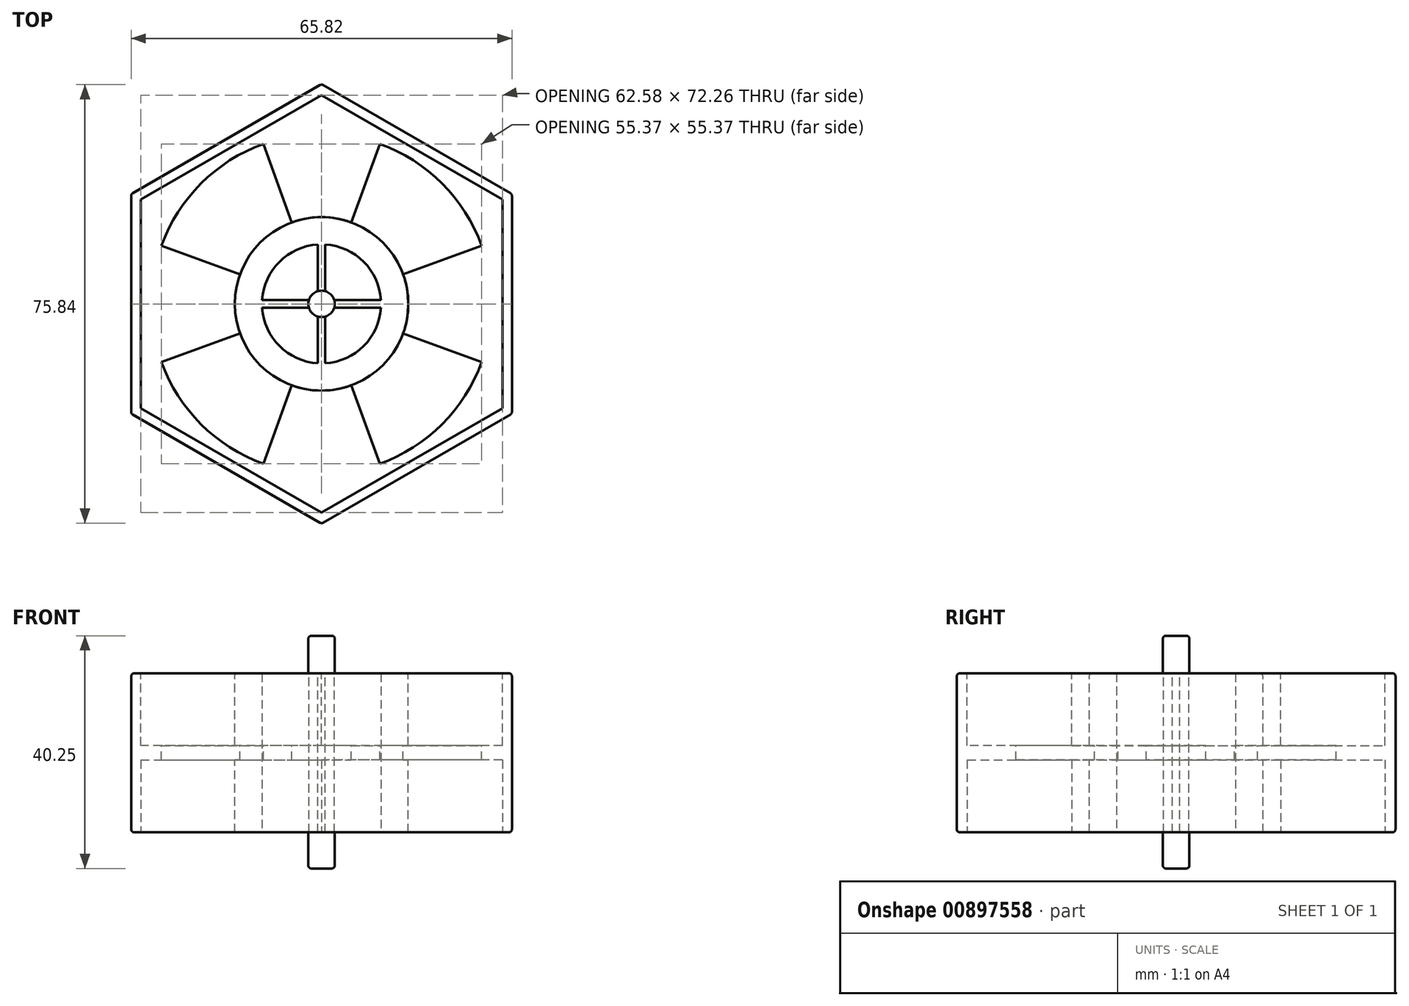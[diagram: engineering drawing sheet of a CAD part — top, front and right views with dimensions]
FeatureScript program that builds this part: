
annotation { "Feature Type Name" : "Feature", "Feature Type Description" : "" }
export const myFeature = defineFeature(function(context is Context, id is Id, definition is map)
    precondition{}
    {
        {
            var Q0;
            Q0=qCreatedBy(makeId("Top.planeOp"),FACE);
            var sketch = newSketch(context, id + "F0", { "sketchPlane" : qUnion([Q0])});
            skCircle(sketch, "E0.cCircle", {"center": v(0, 0) * mm, "radius": 38 * mm, "construction": true});
            skLineSegment(sketch, "E0.0", {"start": v(0, 38) * mm, "end": v(32.9, 19) * mm});
            skLineSegment(sketch, "E0.1", {"start": v(32.9, 19) * mm, "end": v(32.9, -19) * mm});
            skLineSegment(sketch, "E0.2", {"start": v(32.9, -19) * mm, "end": v(0, -38) * mm});
            skLineSegment(sketch, "E0.3", {"start": v(0, -38) * mm, "end": v(-32.9, -19) * mm});
            skLineSegment(sketch, "E0.4", {"start": v(-32.9, -19) * mm, "end": v(-32.9, 19) * mm});
            skLineSegment(sketch, "E0.5", {"start": v(-32.9, 19) * mm, "end": v(0, 38) * mm});
            skSolve(sketch);
        }
        {
            var Q0;
            Q0 = qSketchRegion(id + "F0", true);
            extrude(context, id + "F1", {"entities" : qUnion([Q0]), "depth" : 27.5 * mm, "offsetDistance" : 25 * mm});
        }
        {
            var Q0;
            Q0=makeQuery(id+"F1.opExtrude","CAP_FACE",FACE,{"disambiguationData":[OSD([sQuery(id+"F0.wireOp",EDGE,"E0.0"),sQuery(id+"F0.wireOp",EDGE,"E0.1"),sQuery(id+"F0.wireOp",EDGE,"E0.2"),sQuery(id+"F0.wireOp",EDGE,"E0.3"),sQuery(id+"F0.wireOp",EDGE,"E0.4"),sQuery(id+"F0.wireOp",EDGE,"E0.5")])],"isStart":false});
            var sketch = newSketch(context, id + "F2", { "sketchPlane" : qUnion([Q0])});
            skCircle(sketch, "E1", {"center": v(0, 0) * mm, "radius": 15 * mm});
            skLineSegment(sketch, "E2.0", {"start": v(31.29, -18.06) * mm, "end": v(31.29, 18.06) * mm});
            skLineSegment(sketch, "E2.1", {"start": v(0, 36.13) * mm, "end": v(-31.29, 18.06) * mm});
            skLineSegment(sketch, "E2.2", {"start": v(-31.29, 18.06) * mm, "end": v(-31.29, -18.06) * mm});
            skLineSegment(sketch, "E2.3", {"start": v(31.29, 18.06) * mm, "end": v(0, 36.13) * mm});
            skLineSegment(sketch, "E2.4", {"start": v(-31.29, -18.06) * mm, "end": v(0, -36.13) * mm});
            skLineSegment(sketch, "E2.5", {"start": v(0, -36.13) * mm, "end": v(31.29, -18.06) * mm});
            skSolve(sketch);
        }
        {
            var Q0;
            Q0 = qSketchRegion(id + "F2", true);
            extrude(context, id + "F3", {"entities" : qUnion([Q0]), "operationType" : NewBodyOperationType.REMOVE, "oppositeDirection" : true, "depth" : 12.5 * mm, "offsetDistance" : 25 * mm});
        }
        {
            var Q0;
            Q0=makeQuery(id+"F1.opExtrude","CAP_FACE",FACE,{"disambiguationData":[OSD([sQuery(id+"F0.wireOp",EDGE,"E0.0"),sQuery(id+"F0.wireOp",EDGE,"E0.1"),sQuery(id+"F0.wireOp",EDGE,"E0.2"),sQuery(id+"F0.wireOp",EDGE,"E0.3"),sQuery(id+"F0.wireOp",EDGE,"E0.4"),sQuery(id+"F0.wireOp",EDGE,"E0.5")])],"isStart":true});
            var sketch = newSketch(context, id + "F4", { "sketchPlane" : qUnion([Q0])});
            skLineSegment(sketch, "E3.0", {"start": v(31.29, -18.06) * mm, "end": v(0, -36.13) * mm});
            skLineSegment(sketch, "E4.0", {"start": v(0, -36.13) * mm, "end": v(-31.29, -18.06) * mm});
            skLineSegment(sketch, "E5.0", {"start": v(-31.29, -18.06) * mm, "end": v(-31.29, 18.06) * mm});
            skLineSegment(sketch, "E6.0", {"start": v(-31.29, 18.06) * mm, "end": v(0, 36.13) * mm});
            skLineSegment(sketch, "E7.0", {"start": v(0, 36.13) * mm, "end": v(31.29, 18.06) * mm});
            skLineSegment(sketch, "E8.0", {"start": v(31.29, 18.06) * mm, "end": v(31.29, -18.06) * mm});
            skCircle(sketch, "E9.0", {"center": v(0, 0) * mm, "radius": 15 * mm});
            skSolve(sketch);
        }
        {
            var Q0;
            Q0 = qSketchRegion(id + "F4", true);
            extrude(context, id + "F5", {"entities" : qUnion([Q0]), "operationType" : NewBodyOperationType.REMOVE, "oppositeDirection" : true, "depth" : 12.5 * mm, "offsetDistance" : 25 * mm});
        }
        {
            var Q0;
            Q0=makeQuery(id+"F5.boolean.opBoolean","SPLIT",FACE,{"disambiguationData":[TD([makeQuery(id+"F5.opExtrude","SWEPT_FACE",FACE,{"disambiguationData":[OSD([sQuery(id+"F4.wireOp",EDGE,"E9.0")])]})])],"derivedFrom":makeQuery(id+"F1.opExtrude","CAP_FACE",FACE,{"disambiguationData":[OSD([sQuery(id+"F0.wireOp",EDGE,"E0.0"),sQuery(id+"F0.wireOp",EDGE,"E0.1"),sQuery(id+"F0.wireOp",EDGE,"E0.2"),sQuery(id+"F0.wireOp",EDGE,"E0.3"),sQuery(id+"F0.wireOp",EDGE,"E0.4"),sQuery(id+"F0.wireOp",EDGE,"E0.5")])],"isStart":true})});
            var sketch = newSketch(context, id + "F6", { "sketchPlane" : qUnion([Q0])});
            skArc(sketch, "E10", {"start": v(10.28, 0.64) * mm, "mid": v(7.28, 7.28) * mm, "end": v(0.64, 10.28) * mm});
            skLineSegment(sketch, "E11.left", {"start": v(0.64, -10.28) * mm, "end": v(0.64, -0.64) * mm});
            skLineSegment(sketch, "E11.right", {"start": v(-0.64, -10.28) * mm, "end": v(-0.64, -0.64) * mm});
            skLineSegment(sketch, "E12.bottom", {"start": v(-10.28, 0.64) * mm, "end": v(-0.64, 0.64) * mm});
            skLineSegment(sketch, "E12.top", {"start": v(-10.28, -0.64) * mm, "end": v(-0.64, -0.64) * mm});
            skPoint(sketch, "E13.orphan", {"position": v(13.85, -0.64) * mm});
            skPoint(sketch, "E14.orphan", {"position": v(13.85, 0.64) * mm});
            skArc(sketch, "E15.trimOffspring", {"start": v(-10.28, -0.64) * mm, "mid": v(-7.28, -7.28) * mm, "end": v(-0.64, -10.28) * mm});
            skPoint(sketch, "E16.orphan", {"position": v(-13.85, -0.64) * mm});
            skPoint(sketch, "E17.orphan", {"position": v(-13.85, 0.64) * mm});
            skPoint(sketch, "E18.orphan", {"position": v(0.64, -11.74) * mm});
            skPoint(sketch, "E19.orphan", {"position": v(-0.64, -11.74) * mm});
            skArc(sketch, "E20.trimOffspring", {"start": v(0.64, -10.28) * mm, "mid": v(7.28, -7.28) * mm, "end": v(10.28, -0.64) * mm});
            skArc(sketch, "E21.trimOffspring", {"start": v(-0.64, 10.28) * mm, "mid": v(-7.28, 7.28) * mm, "end": v(-10.28, 0.64) * mm});
            skPoint(sketch, "E22.orphan", {"position": v(0.64, 11.74) * mm});
            skPoint(sketch, "E23.orphan", {"position": v(-0.64, 11.74) * mm});
            skLineSegment(sketch, "E24.trimOffspring", {"start": v(0.64, -0.64) * mm, "end": v(10.28, -0.64) * mm});
            skLineSegment(sketch, "E25.trimOffspring", {"start": v(0.64, 0.64) * mm, "end": v(0.64, 10.28) * mm});
            skLineSegment(sketch, "E26.trimOffspring", {"start": v(-0.64, 0.64) * mm, "end": v(-0.64, 10.28) * mm});
            skLineSegment(sketch, "E27.trimOffspring", {"start": v(0.64, 0.64) * mm, "end": v(10.28, 0.64) * mm});
            skSolve(sketch);
        }
        {
            var Q0;
            Q0 = qSketchRegion(id + "F6", true);
            extrude(context, id + "F7", {"entities" : qUnion([Q0]), "operationType" : NewBodyOperationType.REMOVE, "endBound" : BoundingType.THROUGH_ALL, "oppositeDirection" : true, "depth" : 25 * mm, "offsetDistance" : 25 * mm});
        }
        {
            var Q0;
            Q0=makeQuery(id+"F5.boolean.opBoolean","SPLIT",FACE,{"disambiguationData":[TD([makeQuery(id+"F5.opExtrude","SWEPT_FACE",FACE,{"disambiguationData":[OSD([sQuery(id+"F4.wireOp",EDGE,"E9.0")])]})])],"derivedFrom":makeQuery(id+"F1.opExtrude","CAP_FACE",FACE,{"disambiguationData":[OSD([sQuery(id+"F0.wireOp",EDGE,"E0.0"),sQuery(id+"F0.wireOp",EDGE,"E0.1"),sQuery(id+"F0.wireOp",EDGE,"E0.2"),sQuery(id+"F0.wireOp",EDGE,"E0.3"),sQuery(id+"F0.wireOp",EDGE,"E0.4"),sQuery(id+"F0.wireOp",EDGE,"E0.5")])],"isStart":true})});
            var sketch = newSketch(context, id + "F8", { "sketchPlane" : qUnion([Q0])});
            skCircle(sketch, "E28", {"center": v(0, 0) * mm, "radius": 2.3 * mm});
            skSolve(sketch);
        }
        {
            var Q0;
            Q0 = qSketchRegion(id + "F8", true);
            extrude(context, id + "F9", {"entities" : qUnion([Q0]), "operationType" : NewBodyOperationType.ADD, "depth" : 6.25 * mm, "offsetDistance" : 25 * mm, "hasSecondDirection" : true, "secondDirectionOppositeDirection" : true, "secondDirectionDepth" : 34 * mm});
        }
        {
            var Q0;
            Q0=makeQuery(id+"F5.boolean.opBoolean","COPY",EDGE,{"derivedFrom":makeQuery(id+"F5.opExtrude","CAP_EDGE",EDGE,{"disambiguationData":[OSD([sQuery(id+"F4.wireOp",EDGE,"E9.0")])],"isStart":true})});
            var Q1;
            Q1=makeQuery(id+"F3.boolean.opBoolean","COPY",EDGE,{"derivedFrom":makeQuery(id+"F3.opExtrude","CAP_EDGE",EDGE,{"disambiguationData":[OSD([sQuery(id+"F2.wireOp",EDGE,"E1")])],"isStart":true})});
            var Q2;
            Q2=makeQuery(id+"F9.opExtrude","CAP_EDGE",EDGE,{"disambiguationData":[OSD([sQuery(id+"F8.wireOp",EDGE,"E28")])],"isStart":false});
            var Q3;
            Q3=makeQuery(id+"F9.opExtrude","CAP_FACE",FACE,{"disambiguationData":[OSD([sQuery(id+"F8.wireOp",EDGE,"E28")])],"isStart":true});
            var Q4;
            Q4=makeQuery(id+"F1.opExtrude","SWEPT_FACE",FACE,{"disambiguationData":[OSD([sQuery(id+"F0.wireOp",EDGE,"E0.4")])]});
            var Q5;
            Q5=makeQuery(id+"F1.opExtrude","SWEPT_FACE",FACE,{"disambiguationData":[OSD([sQuery(id+"F0.wireOp",EDGE,"E0.5")])]});
            var Q6;
            Q6=makeQuery(id+"F1.opExtrude","SWEPT_FACE",FACE,{"disambiguationData":[OSD([sQuery(id+"F0.wireOp",EDGE,"E0.0")])]});
            var Q7;
            Q7=makeQuery(id+"F1.opExtrude","SWEPT_FACE",FACE,{"disambiguationData":[OSD([sQuery(id+"F0.wireOp",EDGE,"E0.1")])]});
            var Q8;
            Q8=makeQuery(id+"F1.opExtrude","SWEPT_FACE",FACE,{"disambiguationData":[OSD([sQuery(id+"F0.wireOp",EDGE,"E0.2")])]});
            var Q9;
            Q9=makeQuery(id+"F1.opExtrude","SWEPT_FACE",FACE,{"disambiguationData":[OSD([sQuery(id+"F0.wireOp",EDGE,"E0.3")])]});
            fillet(context, id + "F10", {"entities" : qUnion([Q0, Q1, Q2, Q3, Q4, Q5, Q6, Q7, Q8, Q9]), "radius" : 0.5 * mm, "tangentPropagation" : true, "allowEdgeOverflow" : false});
        }
        {
            var Q0;
            Q0=makeQuery(id+"F3.boolean.opBoolean","COPY",FACE,{"derivedFrom":makeQuery(id+"F3.opExtrude","CAP_FACE",FACE,{"disambiguationData":[OSD([sQuery(id+"F2.wireOp",EDGE,"E1"),sQuery(id+"F2.wireOp",EDGE,"E2.0"),sQuery(id+"F2.wireOp",EDGE,"E2.1"),sQuery(id+"F2.wireOp",EDGE,"E2.2"),sQuery(id+"F2.wireOp",EDGE,"E2.3"),sQuery(id+"F2.wireOp",EDGE,"E2.4"),sQuery(id+"F2.wireOp",EDGE,"E2.5")])],"isStart":false})});
            var sketch = newSketch(context, id + "F11", { "sketchPlane" : qUnion([Q0])});
            skLineSegment(sketch, "E29", {"start": v(-31.29, 0) * mm, "end": v(31.29, 0) * mm, "construction": true});
            skLineSegment(sketch, "E30", {"start": v(0, -36.13) * mm, "end": v(0, 36.13) * mm, "construction": true});
            skArc(sketch, "E31", {"start": v(-27.68, -10.08) * mm, "mid": v(-20.83, -20.83) * mm, "end": v(-10.08, -27.68) * mm});
            skLineSegment(sketch, "E32", {"start": v(-14.1, -5.13) * mm, "end": v(-27.68, -10.08) * mm});
            skLineSegment(sketch, "E33", {"start": v(-5.13, -14.1) * mm, "end": v(-10.08, -27.68) * mm});
            skCircle(sketch, "E34", {"center": v(0, 0) * mm, "radius": 15 * mm});
            skArc(sketch, "E35.1.0", {"start": v(10.08, -27.68) * mm, "mid": v(20.83, -20.83) * mm, "end": v(27.68, -10.08) * mm});
            skLineSegment(sketch, "E35.1.1", {"start": v(5.13, -14.1) * mm, "end": v(10.08, -27.68) * mm});
            skLineSegment(sketch, "E35.1.2", {"start": v(14.1, -5.13) * mm, "end": v(27.68, -10.08) * mm});
            skArc(sketch, "E35.2.0", {"start": v(27.68, 10.08) * mm, "mid": v(20.83, 20.83) * mm, "end": v(10.08, 27.68) * mm});
            skLineSegment(sketch, "E35.2.1", {"start": v(14.1, 5.13) * mm, "end": v(27.68, 10.08) * mm});
            skLineSegment(sketch, "E35.2.2", {"start": v(5.13, 14.1) * mm, "end": v(10.08, 27.68) * mm});
            skArc(sketch, "E35.3.0", {"start": v(-10.08, 27.68) * mm, "mid": v(-20.83, 20.83) * mm, "end": v(-27.68, 10.08) * mm});
            skLineSegment(sketch, "E35.3.1", {"start": v(-5.13, 14.1) * mm, "end": v(-10.08, 27.68) * mm});
            skLineSegment(sketch, "E35.3.2", {"start": v(-14.1, 5.13) * mm, "end": v(-27.68, 10.08) * mm});
            skSolve(sketch);
        }
        {
            var Q0;
            Q0=makeQuery(id+"F11.imprint","IMPRINT",FACE,{"disambiguationData":[TD([[makeQuery(id+"F11.imprint","IMPRINT",EDGE,{"derivedFrom":sQuery(id+"F11.wireOp",EDGE,"E31")}),1.0]])]});
            var Q1;
            Q1=makeQuery(id+"F11.imprint","IMPRINT",FACE,{"disambiguationData":[TD([[makeQuery(id+"F11.imprint","IMPRINT",EDGE,{"derivedFrom":sQuery(id+"F11.wireOp",EDGE,"E35.3.0")}),1.0]])]});
            var Q2;
            Q2=makeQuery(id+"F11.imprint","IMPRINT",FACE,{"disambiguationData":[TD([[makeQuery(id+"F11.imprint","IMPRINT",EDGE,{"derivedFrom":sQuery(id+"F11.wireOp",EDGE,"E35.2.0")}),1.0]])]});
            var Q3;
            Q3=makeQuery(id+"F11.imprint","IMPRINT",FACE,{"disambiguationData":[TD([[makeQuery(id+"F11.imprint","IMPRINT",EDGE,{"derivedFrom":sQuery(id+"F11.wireOp",EDGE,"E35.1.0")}),1.0]])]});
            extrude(context, id + "F12", {"entities" : qUnion([Q0, Q1, Q2, Q3]), "operationType" : NewBodyOperationType.REMOVE, "endBound" : BoundingType.THROUGH_ALL, "oppositeDirection" : true, "depth" : 25 * mm, "offsetDistance" : 25 * mm});
        }
    });
